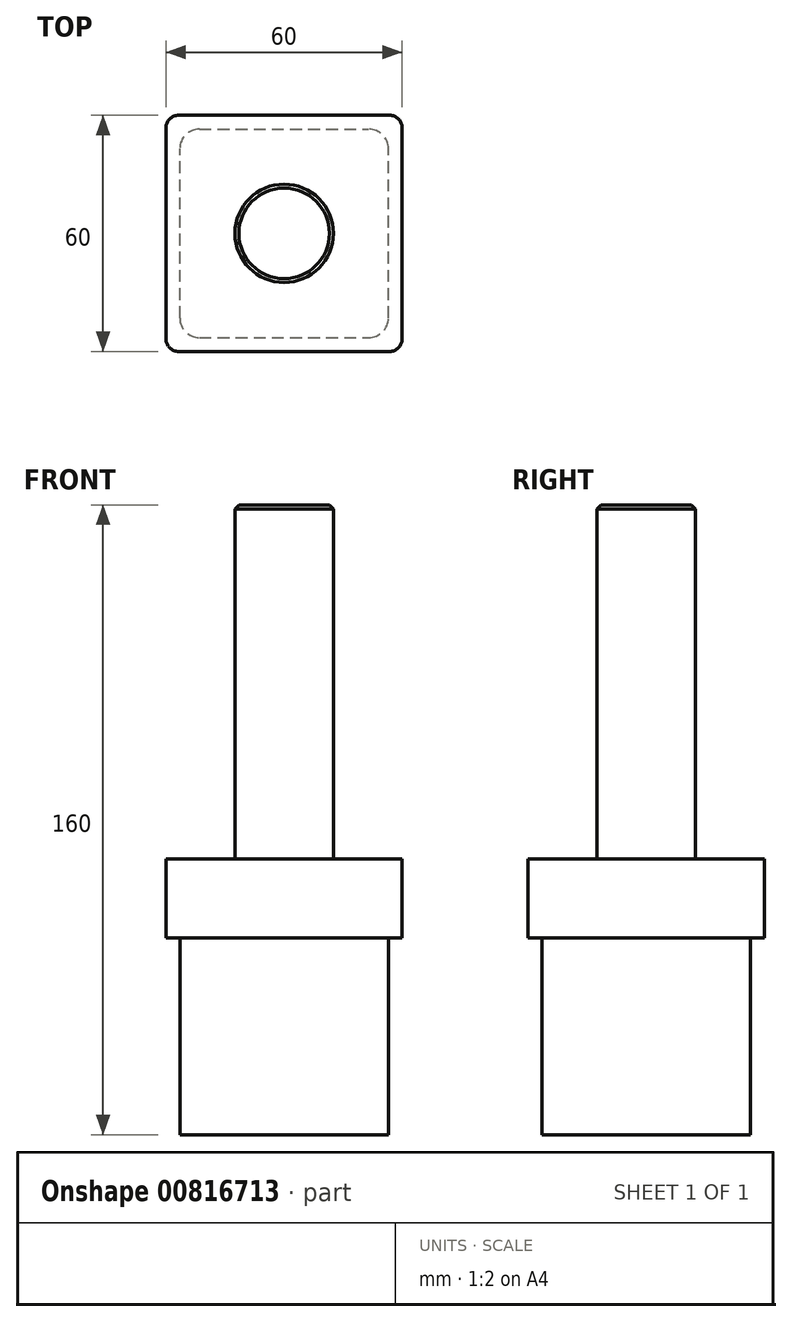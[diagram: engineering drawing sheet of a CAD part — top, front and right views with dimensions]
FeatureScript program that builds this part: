
annotation { "Feature Type Name" : "Feature", "Feature Type Description" : "" }
export const myFeature = defineFeature(function(context is Context, id is Id, definition is map)
    precondition{}
    {
        {
            var Q0;
            Q0=qCreatedBy(makeId("Top.planeOp"),FACE);
            var sketch = newSketch(context, id + "F0", { "sketchPlane" : qUnion([Q0])});
            skLineSegment(sketch, "E0.bottom", {"start": v(-56.8, 0) * mm, "end": v(-3.2, 0) * mm});
            skLineSegment(sketch, "E0.top", {"start": v(-56.8, 60) * mm, "end": v(-3.2, 60) * mm});
            skLineSegment(sketch, "E0.left", {"start": v(-60, 3.2) * mm, "end": v(-60, 56.8) * mm});
            skLineSegment(sketch, "E0.right", {"start": v(0, 3.2) * mm, "end": v(0, 56.8) * mm});
            skPoint(sketch, "E1.visualSharp", {"position": v(-60, 60) * mm});
            skArc(sketch, "E1.filletArc", {"start": v(-56.8, 60) * mm, "mid": v(-59.06, 59.06) * mm, "end": v(-60, 56.8) * mm});
            skPoint(sketch, "E2.visualSharp", {"position": v(0, 60) * mm});
            skArc(sketch, "E2.filletArc", {"start": v(0, 56.8) * mm, "mid": v(-0.94, 59.06) * mm, "end": v(-3.2, 60) * mm});
            skPoint(sketch, "E3.visualSharp", {"position": v(0, 0) * mm});
            skArc(sketch, "E3.filletArc", {"start": v(-3.2, 0) * mm, "mid": v(-0.94, 0.94) * mm, "end": v(0, 3.2) * mm});
            skPoint(sketch, "E4.visualSharp", {"position": v(-60, 0) * mm});
            skArc(sketch, "E4.filletArc", {"start": v(-60, 3.2) * mm, "mid": v(-59.06, 0.94) * mm, "end": v(-56.8, 0) * mm});
            skSolve(sketch);
        }
        {
            var Q0;
            Q0=makeQuery(id+"F0.imprint","IMPRINT",FACE,{"disambiguationData":[TD([[makeQuery(id+"F0.imprint","IMPRINT",EDGE,{"derivedFrom":sQuery(id+"F0.wireOp",EDGE,"E0.bottom")}),1.0]])]});
            extrude(context, id + "F1", {"entities" : qUnion([Q0]), "depth" : 70 * mm, "offsetDistance" : 25 * mm});
        }
        {
            var Q0;
            Q0=makeQuery(id+"F1.opExtrude","CAP_FACE",FACE,{"disambiguationData":[OSD([sQuery(id+"F0.wireOp",EDGE,"E0.bottom"),sQuery(id+"F0.wireOp",EDGE,"E0.top"),sQuery(id+"F0.wireOp",EDGE,"E0.left"),sQuery(id+"F0.wireOp",EDGE,"E0.right"),sQuery(id+"F0.wireOp",EDGE,"E1.filletArc"),sQuery(id+"F0.wireOp",EDGE,"E2.filletArc"),sQuery(id+"F0.wireOp",EDGE,"E3.filletArc"),sQuery(id+"F0.wireOp",EDGE,"E4.filletArc")])],"isStart":true});
            var sketch = newSketch(context, id + "F2", { "sketchPlane" : qUnion([Q0])});
            skLineSegment(sketch, "E5.bottom", {"start": v(-56.5, -3.5) * mm, "end": v(-3.5, -3.5) * mm});
            skLineSegment(sketch, "E5.top", {"start": v(-56.5, -56.5) * mm, "end": v(-3.5, -56.5) * mm});
            skLineSegment(sketch, "E5.left", {"start": v(-56.5, -3.5) * mm, "end": v(-56.5, -56.5) * mm});
            skLineSegment(sketch, "E5.right", {"start": v(-3.5, -3.5) * mm, "end": v(-3.5, -56.5) * mm});
            skSolve(sketch);
        }
        {
            var Q0;
            Q0=makeQuery(id+"F2.imprint","IMPRINT",FACE,{"disambiguationData":[TD([[makeQuery(id+"F2.imprint","IMPRINT",EDGE,{"derivedFrom":sQuery(id+"F2.wireOp",EDGE,"E5.bottom")}),1.0]])]});
            extrude(context, id + "F3", {"entities" : qUnion([Q0]), "operationType" : NewBodyOperationType.REMOVE, "oppositeDirection" : true, "depth" : 50 * mm, "offsetDistance" : 25 * mm});
        }
        {
            var Q0;
            Q0=makeQuery(id+"F3.boolean.opBoolean","COPY",EDGE,{"derivedFrom":makeQuery(id+"F3.opExtrude","SWEPT_EDGE",EDGE,{"disambiguationData":[OSD([sQuery(id+"F2.wireOp",EDGE,"E5.bottom"),sQuery(id+"F2.wireOp",EDGE,"E5.left")])]})});
            var Q1;
            Q1=makeQuery(id+"F3.boolean.opBoolean","COPY",EDGE,{"derivedFrom":makeQuery(id+"F3.opExtrude","SWEPT_EDGE",EDGE,{"disambiguationData":[OSD([sQuery(id+"F2.wireOp",EDGE,"E5.bottom"),sQuery(id+"F2.wireOp",EDGE,"E5.right")])]})});
            var Q2;
            Q2=makeQuery(id+"F3.boolean.opBoolean","COPY",EDGE,{"derivedFrom":makeQuery(id+"F3.opExtrude","SWEPT_EDGE",EDGE,{"disambiguationData":[OSD([sQuery(id+"F2.wireOp",EDGE,"E5.top"),sQuery(id+"F2.wireOp",EDGE,"E5.right")])]})});
            var Q3;
            Q3=makeQuery(id+"F3.boolean.opBoolean","COPY",EDGE,{"derivedFrom":makeQuery(id+"F3.opExtrude","SWEPT_EDGE",EDGE,{"disambiguationData":[OSD([sQuery(id+"F2.wireOp",EDGE,"E5.top"),sQuery(id+"F2.wireOp",EDGE,"E5.left")])]})});
            fillet(context, id + "F4", {"entities" : qUnion([Q0, Q1, Q2, Q3]), "radius" : 5 * mm, "tangentPropagation" : true, "allowEdgeOverflow" : false});
        }
        {
            var Q0;
            Q0=makeQuery(id+"F1.opExtrude","CAP_FACE",FACE,{"disambiguationData":[OSD([sQuery(id+"F0.wireOp",EDGE,"E0.bottom"),sQuery(id+"F0.wireOp",EDGE,"E0.top"),sQuery(id+"F0.wireOp",EDGE,"E0.left"),sQuery(id+"F0.wireOp",EDGE,"E0.right"),sQuery(id+"F0.wireOp",EDGE,"E1.filletArc"),sQuery(id+"F0.wireOp",EDGE,"E2.filletArc"),sQuery(id+"F0.wireOp",EDGE,"E3.filletArc"),sQuery(id+"F0.wireOp",EDGE,"E4.filletArc")])],"isStart":false});
            var sketch = newSketch(context, id + "F5", { "sketchPlane" : qUnion([Q0])});
            skCircle(sketch, "E6", {"center": v(-30, 30) * mm, "radius": 12.5 * mm});
            skSolve(sketch);
        }
        {
            var Q0;
            Q0=makeQuery(id+"F5.imprint","IMPRINT",FACE,{"disambiguationData":[TD([[makeQuery(id+"F5.imprint","IMPRINT",EDGE,{"derivedFrom":sQuery(id+"F5.wireOp",EDGE,"E6")}),1.0]])]});
            extrude(context, id + "F6", {"entities" : qUnion([Q0]), "operationType" : NewBodyOperationType.ADD, "depth" : 90 * mm, "offsetDistance" : 25 * mm});
        }
        {
            var Q0;
            Q0=makeQuery(id+"F6.opExtrude","CAP_EDGE",EDGE,{"disambiguationData":[OSD([sQuery(id+"F5.wireOp",EDGE,"E6")])],"isStart":false});
            chamfer(context, id + "F7", {"entities" : qUnion([Q0]), "width" : 1 * mm, "tangentPropagation" : true});
        }
    });
